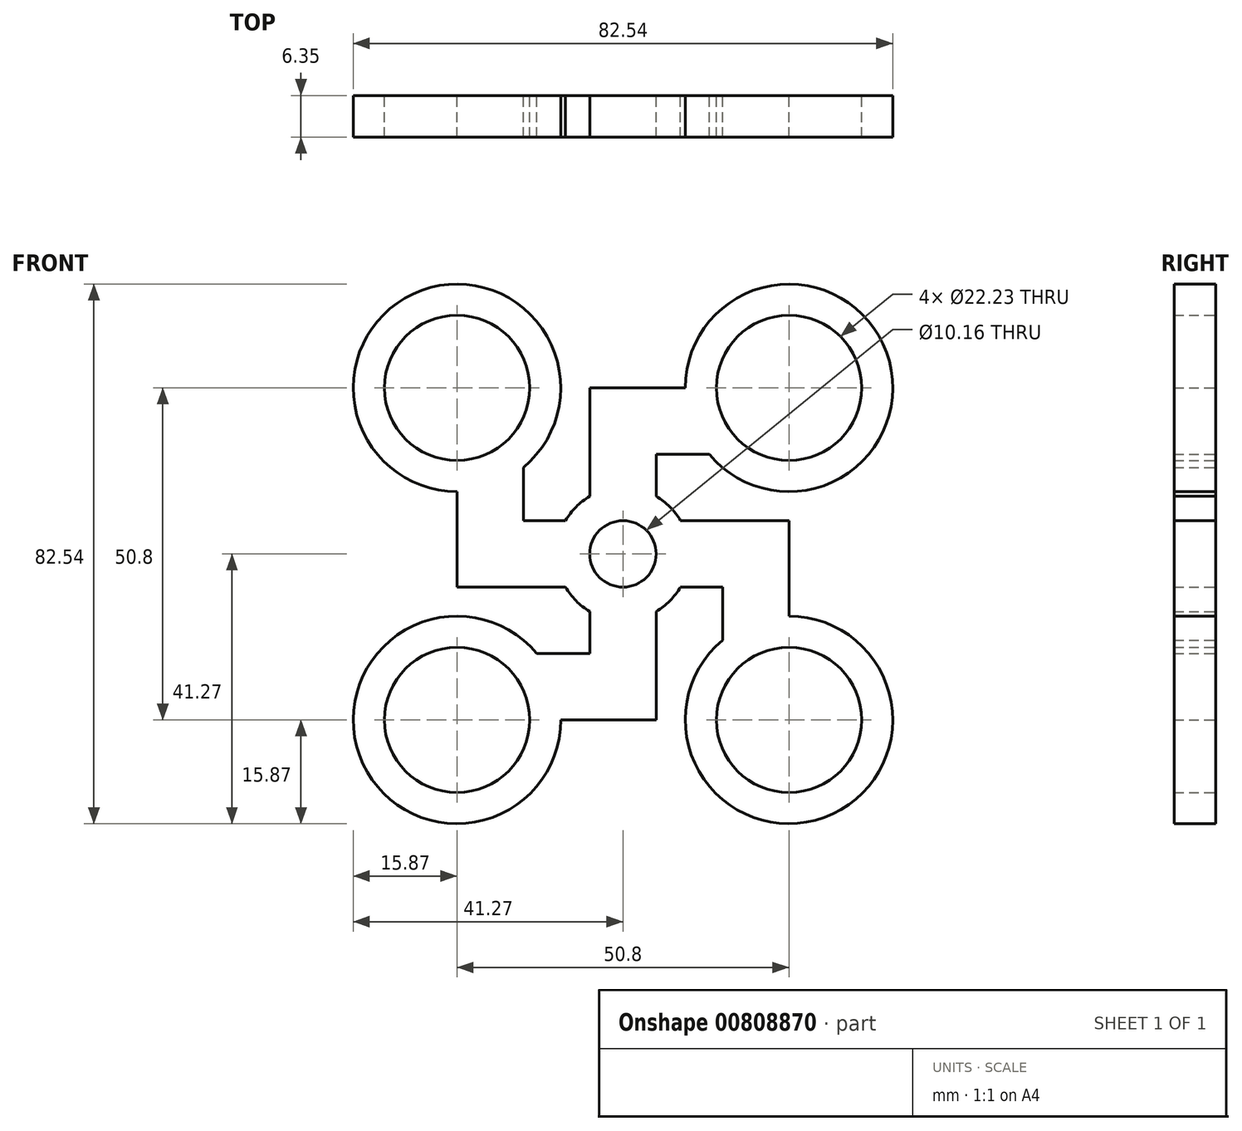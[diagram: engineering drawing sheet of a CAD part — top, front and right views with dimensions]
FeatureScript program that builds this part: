
annotation { "Feature Type Name" : "Feature", "Feature Type Description" : "" }
export const myFeature = defineFeature(function(context is Context, id is Id, definition is map)
    precondition{}
    {
        {
            var Q0;
            Q0=qCreatedBy(makeId("Front.planeOp"),FACE);
            var sketch = newSketch(context, id + "F0", { "sketchPlane" : qUnion([Q0])});
            skLineSegment(sketch, "E0.bottom", {"start": v(25.4, -5.08) * mm, "end": v(-25.4, -5.08) * mm});
            skLineSegment(sketch, "E0.top", {"start": v(25.4, 5.08) * mm, "end": v(-25.4, 5.08) * mm});
            skLineSegment(sketch, "E0.left", {"start": v(25.4, -5.08) * mm, "end": v(25.4, 5.08) * mm});
            skLineSegment(sketch, "E0.right", {"start": v(-25.4, -5.08) * mm, "end": v(-25.4, 5.08) * mm});
            skPoint(sketch, "E0.middle", {"position": v(0, 0) * mm});
            skLineSegment(sketch, "E1", {"start": v(-25.4, 5.08) * mm, "end": v(-25.4, 25.4) * mm});
            skLineSegment(sketch, "E2", {"start": v(-15.24, 25.4) * mm, "end": v(-25.4, 25.4) * mm});
            skLineSegment(sketch, "E3", {"start": v(-15.24, 25.4) * mm, "end": v(-15.24, 5.08) * mm});
            skLineSegment(sketch, "E4", {"start": v(25.4, -5.08) * mm, "end": v(25.4, -25.4) * mm});
            skLineSegment(sketch, "E5", {"start": v(25.4, -25.4) * mm, "end": v(15.24, -25.4) * mm});
            skLineSegment(sketch, "E6", {"start": v(15.24, -25.4) * mm, "end": v(15.24, -5.08) * mm});
            skLineSegment(sketch, "E7.bottom", {"start": v(-5.08, -25.4) * mm, "end": v(5.08, -25.4) * mm});
            skLineSegment(sketch, "E7.top", {"start": v(-5.08, 25.4) * mm, "end": v(5.08, 25.4) * mm});
            skLineSegment(sketch, "E7.left", {"start": v(-5.08, -25.4) * mm, "end": v(-5.08, 25.4) * mm});
            skLineSegment(sketch, "E7.right", {"start": v(5.08, -25.4) * mm, "end": v(5.08, 25.4) * mm});
            skLineSegment(sketch, "E8", {"start": v(5.08, 25.4) * mm, "end": v(25.4, 25.4) * mm});
            skLineSegment(sketch, "E9", {"start": v(25.4, 25.4) * mm, "end": v(25.4, 15.24) * mm});
            skLineSegment(sketch, "E10", {"start": v(25.4, 15.24) * mm, "end": v(5.08, 15.24) * mm});
            skLineSegment(sketch, "E11", {"start": v(-5.08, -25.4) * mm, "end": v(-25.4, -25.4) * mm});
            skLineSegment(sketch, "E12", {"start": v(-25.4, -25.4) * mm, "end": v(-25.4, -15.24) * mm});
            skLineSegment(sketch, "E13", {"start": v(-25.4, -15.24) * mm, "end": v(-5.08, -15.24) * mm});
            skSolve(sketch);
        }
        {
            var Q0;
            Q0 = qSketchRegion(id + "F0", true);
            extrude(context, id + "F1", {"entities" : qUnion([Q0]), "depth" : 6.35 * mm, "offsetDistance" : 25.4 * mm});
        }
        {
            var Q0;
            Q0=qCreatedBy(makeId("Front.planeOp"),FACE);
            var sketch = newSketch(context, id + "F2", { "sketchPlane" : qUnion([Q0])});
            skLineSegment(sketch, "E14", {"start": v(0, 0) * mm, "end": v(0, 25.4) * mm});
            skLineSegment(sketch, "E15", {"start": v(0, 25.4) * mm, "end": v(-25.4, 25.4) * mm});
            skLineSegment(sketch, "E16", {"start": v(0, 25.4) * mm, "end": v(25.4, 25.4) * mm});
            skLineSegment(sketch, "E17", {"start": v(0, 0) * mm, "end": v(0, -25.4) * mm});
            skLineSegment(sketch, "E18", {"start": v(0, -25.4) * mm, "end": v(-25.4, -25.4) * mm});
            skLineSegment(sketch, "E19", {"start": v(0, -25.4) * mm, "end": v(25.4, -25.4) * mm});
            skCircle(sketch, "E20", {"center": v(-25.4, 25.4) * mm, "radius": 15.88 * mm});
            skCircle(sketch, "E21", {"center": v(25.4, -25.4) * mm, "radius": 15.88 * mm});
            skCircle(sketch, "E22", {"center": v(-25.4, -25.4) * mm, "radius": 15.88 * mm});
            skCircle(sketch, "E23", {"center": v(25.4, 25.4) * mm, "radius": 15.88 * mm});
            skSolve(sketch);
        }
        {
            var Q0;
            Q0 = qSketchRegion(id + "F2", true);
            extrude(context, id + "F3", {"entities" : qUnion([Q0]), "operationType" : NewBodyOperationType.ADD, "depth" : 6.35 * mm, "offsetDistance" : 25.4 * mm});
        }
        {
            var Q0;
            Q0=qCreatedBy(makeId("Front.planeOp"),FACE);
            var sketch = newSketch(context, id + "F4", { "sketchPlane" : qUnion([Q0])});
            skLineSegment(sketch, "E24", {"start": v(0, 0) * mm, "end": v(0, 25.4) * mm});
            skLineSegment(sketch, "E25", {"start": v(0, 25.4) * mm, "end": v(-25.4, 25.4) * mm});
            skLineSegment(sketch, "E26", {"start": v(-25.4, 25.4) * mm, "end": v(25.4, 25.4) * mm});
            skLineSegment(sketch, "E27", {"start": v(0, 0) * mm, "end": v(0, -25.4) * mm});
            skLineSegment(sketch, "E28", {"start": v(0, -25.4) * mm, "end": v(-25.4, -25.4) * mm});
            skLineSegment(sketch, "E29", {"start": v(-25.4, -25.4) * mm, "end": v(25.4, -25.4) * mm});
            skCircle(sketch, "E30", {"center": v(25.4, -25.4) * mm, "radius": 11.11 * mm});
            skCircle(sketch, "E31", {"center": v(25.4, 25.4) * mm, "radius": 11.11 * mm});
            skCircle(sketch, "E32", {"center": v(-25.4, 25.4) * mm, "radius": 11.11 * mm});
            skCircle(sketch, "E33", {"center": v(-25.4, -25.4) * mm, "radius": 11.11 * mm});
            skSolve(sketch);
        }
        {
            var Q0;
            Q0 = qSketchRegion(id + "F4", true);
            extrude(context, id + "F5", {"entities" : qUnion([Q0]), "operationType" : NewBodyOperationType.REMOVE, "endBound" : BoundingType.THROUGH_ALL, "depth" : 25.4 * mm, "offsetDistance" : 25.4 * mm});
        }
        {
            var Q0;
            Q0=qCreatedBy(makeId("Front.planeOp"),FACE);
            var sketch = newSketch(context, id + "F6", { "sketchPlane" : qUnion([Q0])});
            skCircle(sketch, "E34", {"center": v(0, 0) * mm, "radius": 10.16 * mm});
            skSolve(sketch);
        }
        {
            var Q0;
            Q0 = qSketchRegion(id + "F6", true);
            extrude(context, id + "F7", {"entities" : qUnion([Q0]), "operationType" : NewBodyOperationType.ADD, "depth" : 6.35 * mm, "offsetDistance" : 25.4 * mm});
        }
        {
            var Q0;
            Q0=qCreatedBy(makeId("Front.planeOp"),FACE);
            var sketch = newSketch(context, id + "F8", { "sketchPlane" : qUnion([Q0])});
            skCircle(sketch, "E35", {"center": v(0, 0) * mm, "radius": 5.08 * mm});
            skSolve(sketch);
        }
        {
            var Q0;
            Q0 = qSketchRegion(id + "F8", true);
            extrude(context, id + "F9", {"entities" : qUnion([Q0]), "operationType" : NewBodyOperationType.REMOVE, "endBound" : BoundingType.THROUGH_ALL, "depth" : 25.4 * mm, "offsetDistance" : 25.4 * mm});
        }
    });
